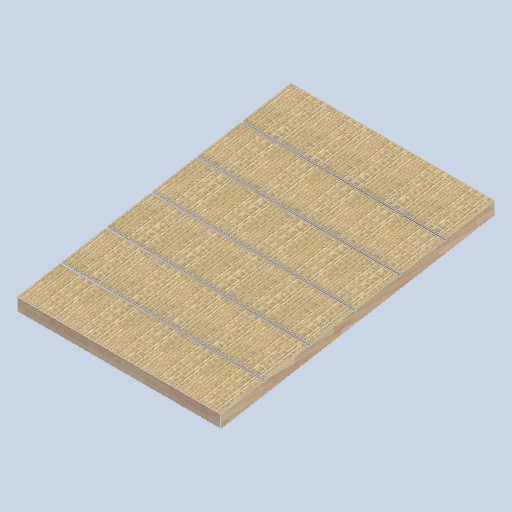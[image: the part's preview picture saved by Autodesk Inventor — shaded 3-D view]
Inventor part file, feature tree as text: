
AUTODESK INVENTOR PART (.ipt)
format: ipt  version: 2024.2 (Build 282272000, 272)  size: 503,296 bytes
history: native  units: mm
features: sketch x5, plane x3, loft x1, extrude x1, projected_geometry x1
ambient origin geometry x8: Origin, YZ Plane, XZ Plane, XY Plane, X Axis, Y Axis, Z Axis, Center Point
bodies: Solid1 (feature_tree)
feature tree (11):
  sketch  "Sketch1"  dims[d0=1644.0mm d1=100.0mm]
  plane  "Work Plane2"
  sketch  "Sketch2"  dims[d2=0.0mm d3=2209.0mm d4=17.453293mm]
  plane  "Work Plane3"
  sketch  "Sketch3"  dims[d5=17.453293mm]
  loft  "Loft1"
  extrude  "Extrusion1"  Depth=2209.0mm
  plane  "Work Plane1"
  sketch  "Sketch4"  dims[d6=1644.0mm]
  sketch  "Sketch5"  dims[d7=0.0mm d8=90.0deg d9=0.0mm d10=90.0deg d11=350.0mm d12=350.0mm d13=350.0mm d14=350.0mm d15=350.0mm d16=0.0mm d17=0.0mm]
  projected_geometry  "Projected Loop1"
